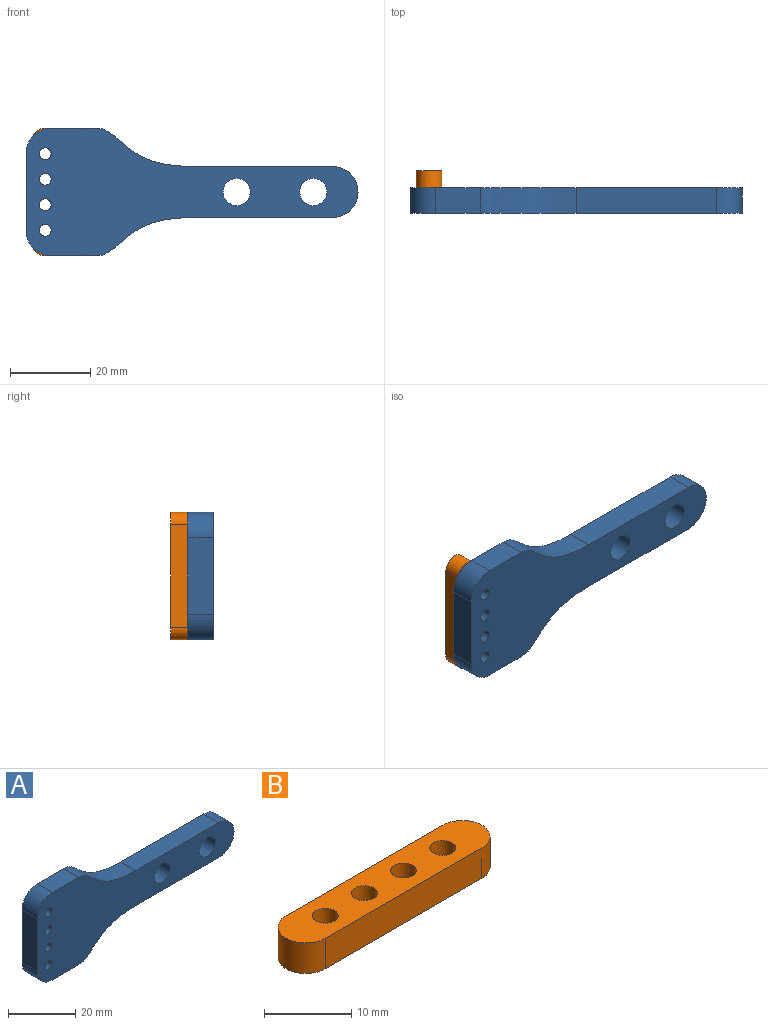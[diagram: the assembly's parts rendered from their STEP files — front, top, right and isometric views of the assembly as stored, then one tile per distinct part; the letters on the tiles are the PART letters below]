
ASSEMBLY  parts=2 mates=1
PART A: 18 faces, bbox 82.6x6.4x31.8 mm
  f0: plane 11.11x6.35mm, normal (0,0,1), area 70.6mm2, adj f1,f2,f5,f16
  f1: plane 82.55x31.75mm, normal (0,-1,0), area 1410.8mm2, adj f0,f3,f4,f5,f6,f7,f8,f9
  f2: plane 82.55x31.75mm, normal (0,1,0), area 1410.8mm2, adj f0,f3,f4,f5,f6,f7,f8,f9
  f3: plane 11.11x6.35mm, normal (0,0,-1), area 70.6mm2, adj f1,f2,f6,f14
  f4: plane 19.05x6.35mm, normal (-1,0,0), area 121mm2, adj f1,f2,f5,f6
  f5: cylinder r=6.35mm len=6.35mm, axis (0,-1,0), area 63.3mm2, adj f0,f1,f2,f4
  f6: cylinder r=6.35mm len=6.35mm, axis (0,-1,0), area 63.3mm2, adj f1,f2,f3,f4
  f7: cylinder r=1.47mm len=6.35mm, axis (0,-1,0), area 58.8mm2, adj f1,f2
  f8: cylinder r=1.47mm len=6.35mm, axis (0,-1,0), area 58.8mm2, adj f1,f2
  f9: cylinder r=1.47mm len=6.35mm, axis (0,-1,0), area 58.8mm2, adj f1,f2
  f10: cylinder r=1.47mm len=6.35mm, axis (0,-1,0), area 58.8mm2, adj f1,f2
  f11: cylinder r=3.38mm len=6.76mm, axis (0,-1,0), area 134.8mm2, adj f1,f2
  f12: cylinder r=3.38mm len=6.76mm, axis (0,-1,0), area 134.8mm2, adj f1,f2
  f13: plane 34.93x6.35mm, normal (0,0,-1), area 221.8mm2, adj f1,f2,f14,f15
  f14: extruded ~23.81x9.53mm, area 167.8mm2, adj f1,f2,f3,f13
  f15: cylinder r=6.35mm len=12.7mm, axis (0,-1,0), area 126.7mm2, adj f1,f2,f13,f17
  f16: extruded ~23.81x9.53mm, area 167.8mm2, adj f0,f1,f2,f17
  f17: plane 34.93x6.35mm, normal (0,0,1), area 221.8mm2, adj f1,f2,f15,f16
PART B: 10 faces, bbox 31.8x6.4x4.3 mm
  f0: plane 31.75x6.35mm, normal (0,0,1), area 165.7mm2, adj f2,f3,f4,f5,f6,f7,f8,f9
  f1: plane 31.75x6.35mm, normal (0,0,-1), area 165.7mm2, adj f2,f3,f4,f5,f6,f7,f8,f9
  f2: plane 25.4x4.27mm, normal (0,-1,0), area 108.4mm2, adj f0,f1,f8,f9
  f3: plane 25.4x4.27mm, normal (0,1,0), area 108.4mm2, adj f0,f1,f8,f9
  f4: cylinder r=1.47mm len=4.27mm, axis (0,0,1), area 39.5mm2, adj f0,f1
  f5: cylinder r=1.47mm len=4.27mm, axis (0,0,1), area 39.5mm2, adj f0,f1
  f6: cylinder r=1.47mm len=4.27mm, axis (0,0,1), area 39.5mm2, adj f0,f1
  f7: cylinder r=1.47mm len=4.27mm, axis (0,0,1), area 39.5mm2, adj f0,f1
  f8: cylinder r=3.17mm len=6.35mm, axis (0,0,1), area 42.6mm2, adj f0,f1,f2,f3
  f9: cylinder r=3.17mm len=6.35mm, axis (0,0,1), area 42.6mm2, adj f0,f1,f2,f3
PLACE A t=(0.22,4.76,2.18)mm
PLACE B rot(axis=(0.58,0.58,-0.58),120deg) t=(-36.28,9.02,2.18)mm
MATE fastened B.f4 <-> A.f7  axis (0,-1,0) through (-36.28,4.76,11.7)mm
